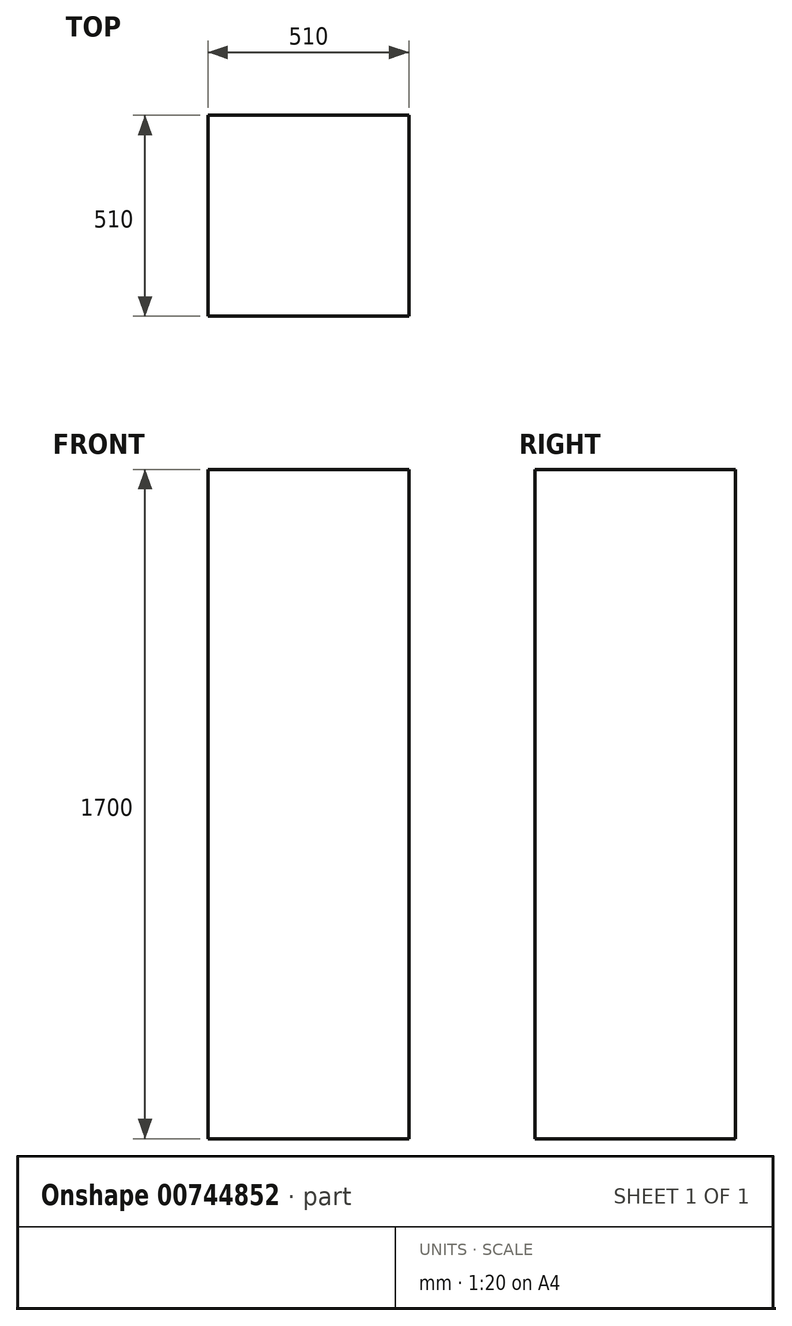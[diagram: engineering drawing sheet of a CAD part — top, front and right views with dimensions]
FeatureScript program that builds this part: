
annotation { "Feature Type Name" : "Feature", "Feature Type Description" : "" }
export const myFeature = defineFeature(function(context is Context, id is Id, definition is map)
    precondition{}
    {
        {
            var Q0;
            Q0=qCreatedBy(makeId("Top.planeOp"),FACE);
            var sketch = newSketch(context, id + "F0", { "sketchPlane" : qUnion([Q0])});
            skLineSegment(sketch, "E0.bottom", {"start": v(0, 0) * mm, "end": v(510, 0) * mm});
            skLineSegment(sketch, "E0.top", {"start": v(0, 510) * mm, "end": v(510, 510) * mm});
            skLineSegment(sketch, "E0.left", {"start": v(0, 0) * mm, "end": v(0, 510) * mm});
            skLineSegment(sketch, "E0.right", {"start": v(510, 0) * mm, "end": v(510, 510) * mm});
            skSolve(sketch);
        }
        {
            var Q0;
            Q0=makeQuery(id+"F0.imprint","IMPRINT",FACE,{"disambiguationData":[TD([[makeQuery(id+"F0.imprint","IMPRINT",EDGE,{"derivedFrom":sQuery(id+"F0.wireOp",EDGE,"E0.bottom")}),1.0]])]});
            extrude(context, id + "F1", {"entities" : qUnion([Q0]), "depth" : 1700 * mm, "offsetDistance" : 25 * mm});
        }
    });
